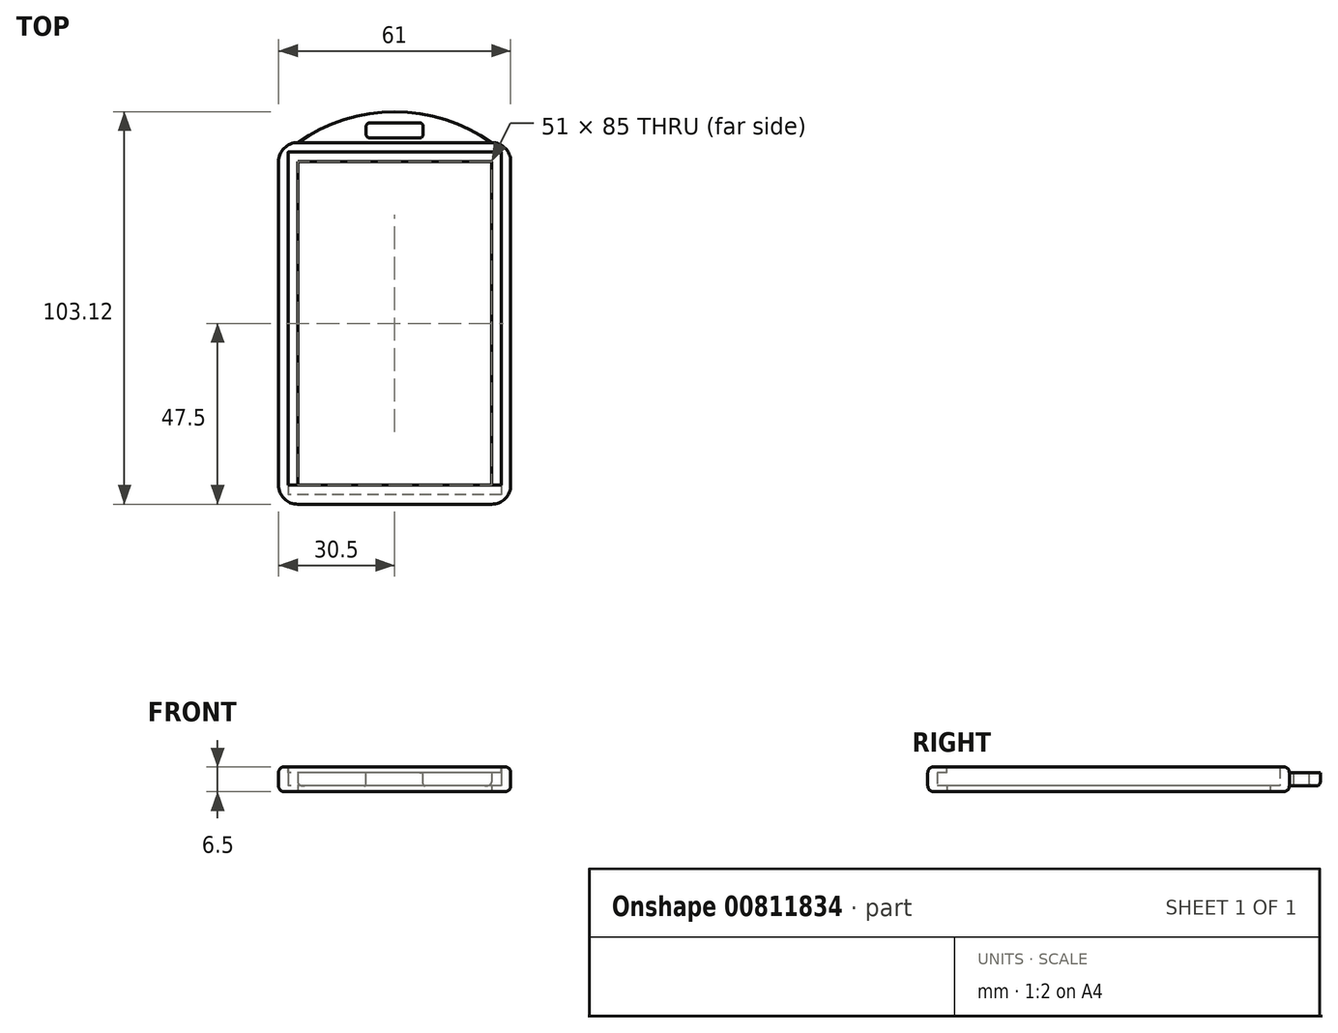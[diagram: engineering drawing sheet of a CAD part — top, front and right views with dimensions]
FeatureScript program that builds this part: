
annotation { "Feature Type Name" : "Feature", "Feature Type Description" : "" }
export const myFeature = defineFeature(function(context is Context, id is Id, definition is map)
    precondition{}
    {
        {
            assignVariable(context, id + "F0", {"name" : "CardThickness", "anyValue" : 3.5});
        }
        {
            assignVariable(context, id + "F1", {"name" : "LipThickness", "anyValue" : 1.5});
        }
        {
            var Q0;
            Q0=qCreatedBy(makeId("Top.planeOp"),FACE);
            var sketch = newSketch(context, id + "F2", { "sketchPlane" : qUnion([Q0])});
            skLineSegment(sketch, "E0.bottom", {"start": v(28, 45) * mm, "end": v(-28, 45) * mm});
            skLineSegment(sketch, "E0.top", {"start": v(28, -45) * mm, "end": v(-28, -45) * mm});
            skLineSegment(sketch, "E0.left", {"start": v(28, 45) * mm, "end": v(28, -45) * mm});
            skLineSegment(sketch, "E0.right", {"start": v(-28, 45) * mm, "end": v(-28, -45) * mm});
            skPoint(sketch, "E0.middle", {"position": v(0, 0) * mm});
            skLineSegment(sketch, "E1.0", {"start": v(25.5, 47.5) * mm, "end": v(-25.5, 47.5) * mm});
            skLineSegment(sketch, "E1.1", {"start": v(30.5, 42.5) * mm, "end": v(30.5, -42.5) * mm});
            skLineSegment(sketch, "E1.2", {"start": v(25.5, -47.5) * mm, "end": v(-25.5, -47.5) * mm});
            skLineSegment(sketch, "E1.3", {"start": v(-30.5, 42.5) * mm, "end": v(-30.5, -42.5) * mm});
            skPoint(sketch, "E2.visualSharp", {"position": v(-30.5, 47.5) * mm});
            skArc(sketch, "E2.filletArc", {"start": v(-25.5, 47.5) * mm, "mid": v(-29.04, 46.04) * mm, "end": v(-30.5, 42.5) * mm});
            skPoint(sketch, "E3.visualSharp", {"position": v(30.5, 47.5) * mm});
            skArc(sketch, "E3.filletArc", {"start": v(30.5, 42.5) * mm, "mid": v(29.04, 46.04) * mm, "end": v(25.5, 47.5) * mm});
            skPoint(sketch, "E4.visualSharp", {"position": v(30.5, -47.5) * mm});
            skArc(sketch, "E4.filletArc", {"start": v(25.5, -47.5) * mm, "mid": v(29.04, -46.04) * mm, "end": v(30.5, -42.5) * mm});
            skPoint(sketch, "E5.visualSharp", {"position": v(-30.5, -47.5) * mm});
            skArc(sketch, "E5.filletArc", {"start": v(-30.5, -42.5) * mm, "mid": v(-29.04, -46.04) * mm, "end": v(-25.5, -47.5) * mm});
            skLineSegment(sketch, "E6.0", {"start": v(25.5, -42.5) * mm, "end": v(-25.5, -42.5) * mm});
            skLineSegment(sketch, "E6.1", {"start": v(25.5, 42.5) * mm, "end": v(25.5, -42.5) * mm});
            skLineSegment(sketch, "E6.2", {"start": v(25.5, 42.5) * mm, "end": v(-25.5, 42.5) * mm});
            skLineSegment(sketch, "E6.3", {"start": v(-25.5, 42.5) * mm, "end": v(-25.5, -42.5) * mm});
            skSolve(sketch);
        }
        {
            var Q0;
            Q0=makeQuery(id+"F2.imprint","IMPRINT",FACE,{"disambiguationData":[TD([[makeQuery(id+"F2.imprint","IMPRINT",EDGE,{"derivedFrom":sQuery(id+"F2.wireOp",EDGE,"E0.bottom")}),-1.0]])]});
            extrude(context, id + "F3", {"entities" : qUnion([Q0]), "depth" : ((getVariable(context, 'CardThickness') + (2 * getVariable(context, 'LipThickness')))) * mm, "offsetDistance" : 25 * mm});
        }
        {
            var Q0;
            Q0=makeQuery(id+"F2.imprint","IMPRINT",FACE,{"disambiguationData":[TD([[makeQuery(id+"F2.imprint","IMPRINT",EDGE,{"derivedFrom":sQuery(id+"F2.wireOp",EDGE,"E0.bottom")}),1.0]])]});
            extrude(context, id + "F4", {"entities" : qUnion([Q0]), "operationType" : NewBodyOperationType.ADD, "depth" : (getVariable(context, 'LipThickness')) * mm, "offsetDistance" : 25 * mm});
        }
        {
            var Q0;
            Q0=makeQuery(id+"F3.opExtrude","CAP_FACE",FACE,{"disambiguationData":[OSD([sQuery(id+"F2.wireOp",EDGE,"E0.bottom"),sQuery(id+"F2.wireOp",EDGE,"E0.top"),sQuery(id+"F2.wireOp",EDGE,"E0.left"),sQuery(id+"F2.wireOp",EDGE,"E0.right"),sQuery(id+"F2.wireOp",EDGE,"E1.0"),sQuery(id+"F2.wireOp",EDGE,"E1.1"),sQuery(id+"F2.wireOp",EDGE,"E1.2"),sQuery(id+"F2.wireOp",EDGE,"E1.3"),sQuery(id+"F2.wireOp",EDGE,"E2.filletArc"),sQuery(id+"F2.wireOp",EDGE,"E3.filletArc"),sQuery(id+"F2.wireOp",EDGE,"E4.filletArc"),sQuery(id+"F2.wireOp",EDGE,"E5.filletArc")])],"isStart":false});
            var sketch = newSketch(context, id + "F5", { "sketchPlane" : qUnion([Q0])});
            skLineSegment(sketch, "E7.bottom", {"start": v(-28, -45) * mm, "end": v(28, -45) * mm});
            skLineSegment(sketch, "E7.top", {"start": v(-28, -42.5) * mm, "end": v(28, -42.5) * mm});
            skLineSegment(sketch, "E7.left", {"start": v(-28, -45) * mm, "end": v(-28, -42.5) * mm});
            skLineSegment(sketch, "E7.right", {"start": v(28, -45) * mm, "end": v(28, -42.5) * mm});
            skLineSegment(sketch, "E8.bottom", {"start": v(-28, -42.5) * mm, "end": v(-25.5, -42.5) * mm});
            skLineSegment(sketch, "E8.top", {"start": v(-28, 0) * mm, "end": v(-25.5, 0) * mm});
            skLineSegment(sketch, "E8.left", {"start": v(-28, -42.5) * mm, "end": v(-28, 0) * mm});
            skLineSegment(sketch, "E8.right", {"start": v(-25.5, -42.5) * mm, "end": v(-25.5, 0) * mm});
            skLineSegment(sketch, "E9.bottom", {"start": v(28, -42.5) * mm, "end": v(25.5, -42.5) * mm});
            skLineSegment(sketch, "E9.top", {"start": v(28, 0) * mm, "end": v(25.5, 0) * mm});
            skLineSegment(sketch, "E9.left", {"start": v(28, -42.5) * mm, "end": v(28, 0) * mm});
            skLineSegment(sketch, "E9.right", {"start": v(25.5, -42.5) * mm, "end": v(25.5, 0) * mm});
            skSolve(sketch);
        }
        {
            var Q0;
            Q0=makeQuery(id+"F5.imprint","IMPRINT",FACE,{"disambiguationData":[TD([[makeQuery(id+"F5.imprint","IMPRINT",EDGE,{"derivedFrom":sQuery(id+"F5.wireOp",EDGE,"E8.bottom")}),1.0]])]});
            var Q1;
            Q1=makeQuery(id+"F5.imprint","IMPRINT",FACE,{"disambiguationData":[TD([[makeQuery(id+"F5.imprint","IMPRINT",EDGE,{"derivedFrom":sQuery(id+"F5.wireOp",EDGE,"E7.bottom")}),-1.0]])]});
            var Q2;
            Q2=makeQuery(id+"F5.imprint","IMPRINT",FACE,{"disambiguationData":[TD([[makeQuery(id+"F5.imprint","IMPRINT",EDGE,{"derivedFrom":sQuery(id+"F5.wireOp",EDGE,"E9.bottom")}),-1.0]])]});
            extrude(context, id + "F6", {"entities" : qUnion([Q0, Q1, Q2]), "operationType" : NewBodyOperationType.ADD, "oppositeDirection" : true, "depth" : getVariable(context, 'LipThickness') * mm, "offsetDistance" : 25 * mm});
        }
        {
            var Q0;
            Q0=makeQuery(id+"F3.opExtrude","CAP_EDGE",EDGE,{"disambiguationData":[OSD([sQuery(id+"F2.wireOp",EDGE,"E1.3")])],"isStart":false});
            var Q1;
            Q1=makeQuery(id+"F3.opExtrude","CAP_EDGE",EDGE,{"disambiguationData":[OSD([sQuery(id+"F2.wireOp",EDGE,"E1.1")])],"isStart":true});
            fillet(context, id + "F7", {"entities" : qUnion([Q0, Q1]), "radius" : 1.5 * mm, "tangentPropagation" : true, "allowEdgeOverflow" : false});
        }
        {
            var Q0;
            Q0=makeQuery(id+"F3.opExtrude","SWEPT_FACE",FACE,{"disambiguationData":[OSD([sQuery(id+"F2.wireOp",EDGE,"E1.0")])]});
            extrude(context, id + "F8", {"entities" : qUnion([Q0]), "operationType" : NewBodyOperationType.ADD, "depth" : 10 * mm, "offsetDistance" : 25 * mm});
        }
        {
            var Q0;
            {var subQ0=sQuery(id+"F2.wireOp",EDGE,"E1.0");Q0=makeQuery(id+"F8.opExtrude","SWEPT_FACE",FACE,{"disambiguationData":[OSD([subQ0]),TDD([makeQuery(id+"F7.opFillet","BLEND_EDGE",EDGE,{"blendedFrom":[makeQuery(id+"F3.opExtrude","CAP_EDGE",EDGE,{"disambiguationData":[OSD([subQ0])],"isStart":false}),makeQuery(id+"F3.opExtrude","SWEPT_FACE",FACE,{"disambiguationData":[OSD([subQ0])]})],"blendedInto":[makeQuery(id+"F3.opExtrude","SWEPT_FACE",FACE,{"disambiguationData":[OSD([subQ0])]})]})])]});}
            var sketch = newSketch(context, id + "F9", { "sketchPlane" : qUnion([Q0])});
            skLineSegment(sketch, "E10.bottom", {"start": v(7.5, 52.7) * mm, "end": v(-7.5, 52.7) * mm});
            skLineSegment(sketch, "E10.top", {"start": v(7.5, 48.7) * mm, "end": v(-7.5, 48.7) * mm});
            skLineSegment(sketch, "E10.left", {"start": v(7.5, 52.7) * mm, "end": v(7.5, 48.7) * mm});
            skLineSegment(sketch, "E10.right", {"start": v(-7.5, 52.7) * mm, "end": v(-7.5, 48.7) * mm});
            skArc(sketch, "E11", {"start": v(25.5, 47.5) * mm, "mid": v(0, 55.62) * mm, "end": v(-25.5, 47.5) * mm});
            skSolve(sketch);
        }
        {
            var Q0;
            Q0=makeQuery(id+"F9.imprint","IMPRINT",FACE,{"disambiguationData":[TD([[makeQuery(id+"F9.imprint","IMPRINT",EDGE,{"derivedFrom":sQuery(id+"F9.wireOp",EDGE,"E11")}),-1.0]])]});
            extrude(context, id + "F10", {"entities" : qUnion([Q0]), "operationType" : NewBodyOperationType.REMOVE, "oppositeDirection" : true, "depth" : 25 * mm, "offsetDistance" : 25 * mm});
        }
        {
            var Q0;
            Q0=qSketchRegion(id+"F9",true);
            extrude(context, id + "F11", {"entities" : qUnion([Q0]), "operationType" : NewBodyOperationType.REMOVE, "oppositeDirection" : true, "depth" : 25 * mm, "offsetDistance" : 25 * mm});
        }
        {
            var Q0;
            {var subQ0=sQuery(id+"F2.wireOp",EDGE,"E1.0");Q0=makeQuery(id+"F10.boolean.opBoolean","INTERSECT",EDGE,{"derivedFrom":[makeQuery(id+"F8.opExtrude","SWEPT_FACE",FACE,{"disambiguationData":[OSD([subQ0]),TDD([makeQuery(id+"F7.opFillet","BLEND_EDGE",EDGE,{"blendedFrom":[makeQuery(id+"F3.opExtrude","CAP_EDGE",EDGE,{"disambiguationData":[OSD([subQ0])],"isStart":true}),makeQuery(id+"F3.opExtrude","SWEPT_FACE",FACE,{"disambiguationData":[OSD([subQ0])]})],"blendedInto":[makeQuery(id+"F3.opExtrude","SWEPT_FACE",FACE,{"disambiguationData":[OSD([subQ0])]})]})])]}),makeQuery(id+"F10.opExtrude","SWEPT_FACE",FACE,{"disambiguationData":[OSD([sQuery(id+"F9.wireOp",EDGE,"E11")])]})]});}
            var Q1;
            Q1=makeQuery(id+"F10.boolean.opBoolean","COPY",EDGE,{"derivedFrom":makeQuery(id+"F10.opExtrude","CAP_EDGE",EDGE,{"disambiguationData":[OSD([sQuery(id+"F9.wireOp",EDGE,"E11")])],"isStart":true})});
            fillet(context, id + "F12", {"entities" : qUnion([Q0, Q1]), "radius" : 1 * mm, "tangentPropagation" : true, "allowEdgeOverflow" : false});
        }
        {
            var Q0;
            Q0=makeQuery(id+"F11.boolean.opBoolean","COPY",EDGE,{"derivedFrom":makeQuery(id+"F11.opExtrude","SWEPT_EDGE",EDGE,{"disambiguationData":[OSD([sQuery(id+"F9.wireOp",EDGE,"E10.bottom"),sQuery(id+"F9.wireOp",EDGE,"E10.right")])]})});
            var Q1;
            Q1=makeQuery(id+"F11.boolean.opBoolean","COPY",EDGE,{"derivedFrom":makeQuery(id+"F11.opExtrude","SWEPT_EDGE",EDGE,{"disambiguationData":[OSD([sQuery(id+"F9.wireOp",EDGE,"E10.bottom"),sQuery(id+"F9.wireOp",EDGE,"E10.left")])]})});
            var Q2;
            Q2=makeQuery(id+"F11.boolean.opBoolean","COPY",EDGE,{"derivedFrom":makeQuery(id+"F11.opExtrude","SWEPT_EDGE",EDGE,{"disambiguationData":[OSD([sQuery(id+"F9.wireOp",EDGE,"E10.top"),sQuery(id+"F9.wireOp",EDGE,"E10.left")])]})});
            var Q3;
            Q3=makeQuery(id+"F11.boolean.opBoolean","COPY",EDGE,{"derivedFrom":makeQuery(id+"F11.opExtrude","SWEPT_EDGE",EDGE,{"disambiguationData":[OSD([sQuery(id+"F9.wireOp",EDGE,"E10.top"),sQuery(id+"F9.wireOp",EDGE,"E10.right")])]})});
            fillet(context, id + "F13", {"entities" : qUnion([Q0, Q1, Q2, Q3]), "radius" : 1 * mm, "tangentPropagation" : true, "allowEdgeOverflow" : false});
        }
        {
            var Q0;
            Q0=makeQuery(id+"F11.boolean.opBoolean","COPY",EDGE,{"derivedFrom":makeQuery(id+"F11.opExtrude","CAP_EDGE",EDGE,{"disambiguationData":[OSD([sQuery(id+"F9.wireOp",EDGE,"E10.bottom")])],"isStart":true})});
            var Q1;
            {var subQ0=sQuery(id+"F2.wireOp",EDGE,"E1.0");Q1=makeQuery(id+"F11.boolean.opBoolean","INTERSECT",EDGE,{"derivedFrom":[makeQuery(id+"F8.opExtrude","SWEPT_FACE",FACE,{"disambiguationData":[OSD([subQ0]),TDD([makeQuery(id+"F7.opFillet","BLEND_EDGE",EDGE,{"blendedFrom":[makeQuery(id+"F3.opExtrude","CAP_EDGE",EDGE,{"disambiguationData":[OSD([subQ0])],"isStart":true}),makeQuery(id+"F3.opExtrude","SWEPT_FACE",FACE,{"disambiguationData":[OSD([subQ0])]})],"blendedInto":[makeQuery(id+"F3.opExtrude","SWEPT_FACE",FACE,{"disambiguationData":[OSD([subQ0])]})]})])]}),makeQuery(id+"F11.opExtrude","SWEPT_FACE",FACE,{"disambiguationData":[OSD([sQuery(id+"F9.wireOp",EDGE,"E10.bottom")])]})]});}
            fillet(context, id + "F14", {"entities" : qUnion([Q0, Q1]), "radius" : .5 * mm, "tangentPropagation" : true, "allowEdgeOverflow" : false});
        }
    });
